# Revit family: Drain-Floor-Jay_R_Smith-2484_Series
name_source: partatom
category: Plumbing Fixtures
units: mm (PartAtom-declared; Revit-internal decimal feet)

## family parameters
Cut with Voids When Loaded = No
Host = Face
OmniClass Number = 23.70.50.21.24
OmniClass Title = Waste Water Drains
Part Type = Normal
Room Calculation Point = No
Round Connector Dimension = Use Diameter
Shared = Yes

## types (7) — shared parameters
Assembly Code = D2030300
C - Flashing Clamp = No
CIB - Cast Iron Bucket = No
CW Connection = No
Default Elevation = 0"
Description = Heavy Duty Traffic Floor Drains
Finish = Metal-Jay.R.Smith-Acid Resistant Coating
G - Galvanized = No
Grate Finish = Metal-Jay.R.Smith-Cast Iron
HW Connection = No
Height = 8"
Installation Type = Floor Mounted
Length = 24 3/4"
M - Ductile Iron Gate = No
Manufacturer = Jay R. Smith
Material = Metal-Jay.R.Smith-Acid Resistant Coating
Price = Prices may vary. Please consult Manufacturer Representative for most up-to-date price list.
Product Documentation Link = https://www.jrsmith.com
Product Page URL = https://www.jrsmith.com
U - Vandal Proof  Top = No
URL = https://www.jrsmith.com
Vent Connection = No
W - Seepae Holes = No
Waste Connection = Yes
Width = 17 1/2"
zero-valued in all types: CWFU, HWFU, WFU

## per-type parameters (varying)
| type | C- Caulk Outlet | Connection Description | Model | Outlet Diameter | Outlet Radius | T - Threaded Outlet | Type Comments | Waste Connection Diameter | Waste Connection Radius | Y - No-Hub Outlet |
| 2484C03(75) | Yes | 3" Caulk Waste Outlet Connection | 2484C03(75) | 3 1/4" | 1 5/8" | No | 03(75) Caulk 4(100) x 3(75) Reducer | 3" | 1 1/2" | No |
| 2484Y02(50) | No | 2" No-Hub Waste Outlet Connection | 2484Y02(50) | 2 1/4" | 1 1/8" | No | NO-HUB | 2" | 1" | Yes |
| 2484Y03(75) | No | 3" No-Hub Waste Outlet Connection | 2484Y03(75) | 3 1/4" | 1 5/8" | No | NO-HUB | 3" | 1 1/2" | Yes |
| 2484Y04(100) | No | 4" No-Hub Waste Outlet Connection | 2484Y04(100) | 4 1/4" | 2 1/8" | No | NO-HUB | 4" | 2" | Yes |
| 2484T02(50) | No | 2" Threaded Waste Outlet Connection | 2484T02(50) | 2 1/4" | 1 1/8" | Yes | 02(50) Threaded 4(100) x 2(50) Bushing | 2" | 1" | No |
| 2484T03(75) | No | 3" Threaded Waste Outlet Connection | 2484T03(75) | 3 1/4" | 1 5/8" | Yes | 03(75) Threaded 4(100) x 3(75) Bushing | 3" | 1 1/2" | No |
| 2484T04(100) | No | 4" Threaded Waste Outlet Connection | 248T404(100) | 4 1/4" | 2 1/8" | Yes | Threaded | 4" | 2" | No |

## geometry (parser evidence)
native form markers: Sweep x1
no freeform markers — native parametric forms only
